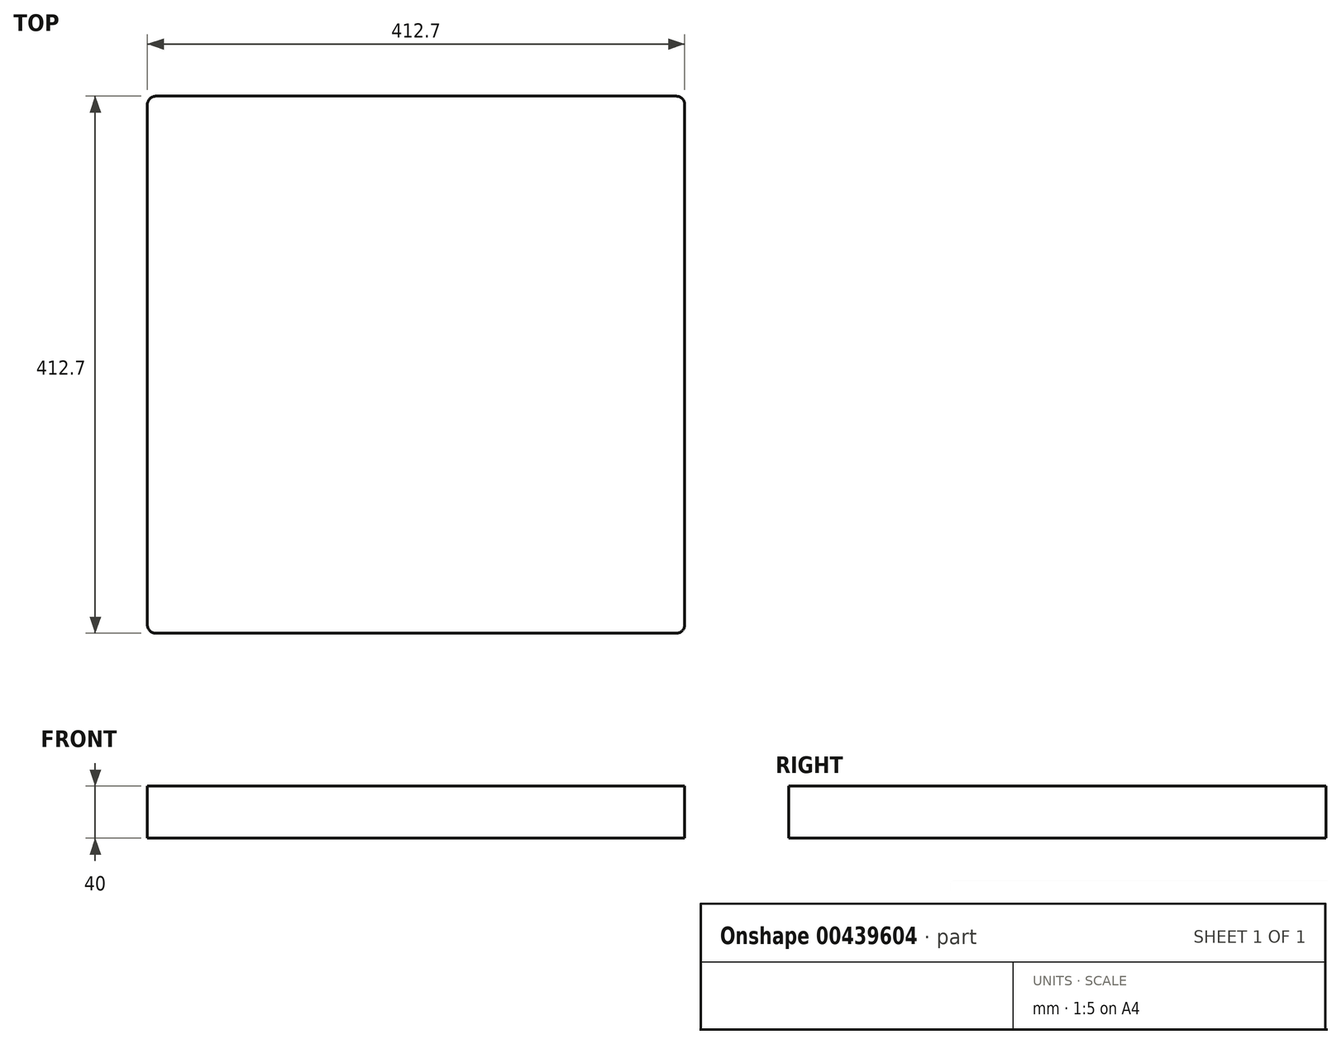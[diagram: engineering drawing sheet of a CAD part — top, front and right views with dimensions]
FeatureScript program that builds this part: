
annotation { "Feature Type Name" : "Feature", "Feature Type Description" : "" }
export const myFeature = defineFeature(function(context is Context, id is Id, definition is map)
    precondition{}
    {
        {
            var Q0;
            Q0=qCreatedBy(makeId("Top.planeOp"),FACE);
            var sketch = newSketch(context, id + "F0", { "sketchPlane" : qUnion([Q0])});
            skLineSegment(sketch, "E0.bottom", {"start": v(-17.77, -382.55) * mm, "end": v(382.23, -382.55) * mm});
            skLineSegment(sketch, "E0.top", {"start": v(-17.77, 30.15) * mm, "end": v(382.23, 30.15) * mm});
            skLineSegment(sketch, "E0.left", {"start": v(-24.12, -376.2) * mm, "end": v(-24.12, 23.8) * mm});
            skLineSegment(sketch, "E0.right", {"start": v(388.58, -376.2) * mm, "end": v(388.58, 23.8) * mm});
            skPoint(sketch, "E1.visualSharp", {"position": v(-24.12, 30.15) * mm});
            skArc(sketch, "E1.filletArc", {"start": v(-17.77, 30.15) * mm, "mid": v(-22.26, 28.3) * mm, "end": v(-24.12, 23.8) * mm});
            skPoint(sketch, "E2.visualSharp", {"position": v(388.58, 30.15) * mm});
            skArc(sketch, "E2.filletArc", {"start": v(388.58, 23.8) * mm, "mid": v(386.72, 28.3) * mm, "end": v(382.23, 30.15) * mm});
            skPoint(sketch, "E3.visualSharp", {"position": v(388.58, -382.55) * mm});
            skArc(sketch, "E3.filletArc", {"start": v(382.23, -382.55) * mm, "mid": v(386.72, -380.69) * mm, "end": v(388.58, -376.2) * mm});
            skPoint(sketch, "E4.visualSharp", {"position": v(-24.12, -382.55) * mm});
            skArc(sketch, "E4.filletArc", {"start": v(-24.12, -376.2) * mm, "mid": v(-22.26, -380.69) * mm, "end": v(-17.77, -382.55) * mm});
            skSolve(sketch);
        }
        {
            var Q0;
            Q0=makeQuery(id+"F0.imprint","IMPRINT",FACE,{"disambiguationData":[TD([[makeQuery(id+"F0.imprint","IMPRINT",EDGE,{"derivedFrom":sQuery(id+"F0.wireOp",EDGE,"E0.bottom")}),1.0]])]});
            extrude(context, id + "F1", {"entities" : qUnion([Q0]), "depth" : 40 * mm});
        }
    });
